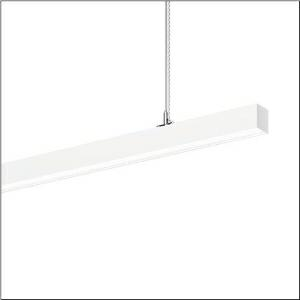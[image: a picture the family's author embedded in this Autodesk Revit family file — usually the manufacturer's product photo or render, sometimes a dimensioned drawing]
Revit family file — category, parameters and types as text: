
# Revit family: silica_21_51mx33db49wb
name_source: partatom
category: Lighting Fixtures
units: mm (PartAtom-declared; Revit-internal decimal feet)

## family parameters
Cut with Voids When Loaded = No
Host = Face
Light Source = No
Part Type = Normal
Room Calculation Point = No
Round Connector Dimension = Use Diameter
Shared = No

## types (1)
- --- (1 x LED, 7390 lm, 48.3 W, 4000K)
    Apparent Load = 48 VA
    CIE Flux Codes = 78 96 99 55 100
    Color Rendering = 80
    Color Temperature = 4000K
    Default Elevation = 1800 mm
    Description = Silica 21, office luminaire, primary optical cover: prismatic diffuser, of PMMA, CAT 2 (L<= 3000cd/m²), light emission: direct/indirect distribution, primary light characteristic: symmetric, installation type: suspended mounting, LED, rated luminous flux: 7.390lm, luminous efficacy: 153lm/W, light colour: 840, colour temperature: 4000K, control gear: DALI 2, with terminal, 3+2-pole, max. 2.5mm², mains connection: 220..240V, AC, 50/60Hz, rated input power: 48.3W, luminaire housing, of aluminium, traffic white (RAL 9016), length: 1.504mm, width: 53mm, height: 53mm, protection rating (complete): IP20, insulation class (complete): insulation class I (protective earthing), certification: CE, permissible operating ambient temperature: 0..+35°C, standard: EN 50419, packaging unit: 1 piece
    Height = 53 mm
    Lamp = 1 x LED
    Lamp Light Flux = 7390 lm
    Lamp Power = 48.3 W
    Lamp count = 1
    Length = 1504 mm
    Luminous efficacy = 153 lm/W
    Manufacturer = Siteco
    ModVariant = No
    Model = 51MX33DB49WB
    Mounting Place = Ceiling
    Mounting Type = Pendant
    Number of Poles = 1
    OnlyDefault = Yes
    Power Factor = 1
    Product Name = Silica 21
    Product group = office luminaire | ceiling pendant
    ProductGroupID = 903
    Protection Class = Protection class I
    Protection Degree = IP 20
    RLX_Detail_Level = 1
    RLX_Emergency_Light_Flux = 0 lm
    RLX_Emergency_Type = 0
    RLX_Emergency_Type_DB = No
    RlxData = <blob elided: 21437 chars, md5=1d7211e8>
    Socket = socket
    Standby Power = 0 W
    System Light Flux = 7390 lm
    System Power = 48 W
    Type Comments = factory setting: luminous flux: 100 % | dim-lin: 254 | 323 mA
    Type Image = l_1349007.jpg
    URL = http://relux.com
    VarID = @adj_118377
    Voltage = 0 V
    Weight = 0.00 kg
    Width = 53 mm

## geometry (parser evidence)
native form markers: Blend x4, Sweep x15
no freeform markers — native parametric forms only
